# Revit family: Bernhardt_Design-Credenzas-Matera-ServingHeight
name_source: partatom
category: Furniture
revit_build: Autodesk Revit 2016 (Build: 20150714_1515(x64)
units: mm (PartAtom-declared; Revit-internal decimal feet)

## family parameters
Always vertical = Yes
Cut with Voids When Loaded = No
OmniClass Number = 23.40.20.00
OmniClass Title = General Furniture and Specialties
Room Calculation Point = No
Shared = No
Work Plane-Based = No

## types (12) — shared parameters
Manufacturer = Bernhardt Design
Matera Metal = <By Category>
Matera Top = <By Category>
Matera Veneer = <By Category>
Model = Matera
Tabletop_depth = 25 3/16"
Tabletop_halfDepth = 12 19/32"
URL = http://www.bernhardtdesign.com
inside_24in-36inDrawers = No
inside_36in-12in = No

## per-type parameters (varying)
| type | Catalog | SKU | Tabletop_halfWidth | Tabletop_width | base_width | inside_18in-18in | inside_20in-20in-20in | inside_24in-24in | inside_24in-24inDrawers | inside_36in-24in | inside_36in-24inDrawers | leg_width | outside | outside_open | subTop_width |
| Matera - TAJ,TIJ | TAJ,TIJ | TAJ,TIJ | 48" | 96" | 42" | No | No | Yes | No | No | No | 24 3/16" | Yes | No | 47 5/32" |
| Matera - TAN,TBN | TAN, TBN | TAN, TBN | 36" | 72" | 30" | Yes | No | No | No | No | No | 18 3/16" | Yes | No | 35 5/32" |
| Matera - TAL,TCL | TAL,TCL | TAL,TCL | 42" | 84" | 36" | No | No | Yes | No | No | No | 24 3/16" | Yes | No | 41 5/32" |
| Matera - TAH,TIH | TAH,TIH | TAH,TIH | 54" | 108" | 48" | No | Yes | No | No | No | No | 30 3/16" | Yes | No | 53 5/32" |
| Matera - TCJ,TEJ | TCJ,TEJ | TCJ,TEJ | 48" | 96" | 42" | No | No | Yes | No | No | No | 24 3/16" | No | Yes | 47 5/32" |
| Matera - TGJ | TGJ | TGJ | 48" | 96" | 42" | No | No | No | No | Yes | No | 30 3/16" | Yes | No | 47 5/32" |
| Matera - THJ | THJ | THJ | 48" | 96" | 42" | No | No | No | Yes | No | No | 30 3/16" | Yes | No | 47 5/32" |
| Matera - TGH | TGH | TGH | 54" | 108" | 48" | No | No | No | No | Yes | No | 30 3/16" | Yes | No | 53 5/32" |
| Matera - THH | THH | THH | 54" | 108" | 48" | No | No | No | No | No | Yes | 30 3/16" | Yes | No | 53 5/32" |
| Matera - TBH,TFH | TBH,TFH | TBH,TFH | 54" | 108" | 48" | No | Yes | No | No | No | No | 30 3/16" | No | Yes | 53 5/32" |
| Matera - TCH | TCH | TCH | 54" | 108" | 48" | No | No | No | No | Yes | No | 30 3/16" | No | Yes | 53 5/32" |
| Matera - TDH | TDH | TDH | 54" | 108" | 48" | No | No | No | No | No | Yes | 30 3/16" | No | Yes | 53 5/32" |

## geometry (parser evidence)
native form markers: Sweep x2
no freeform markers — native parametric forms only
